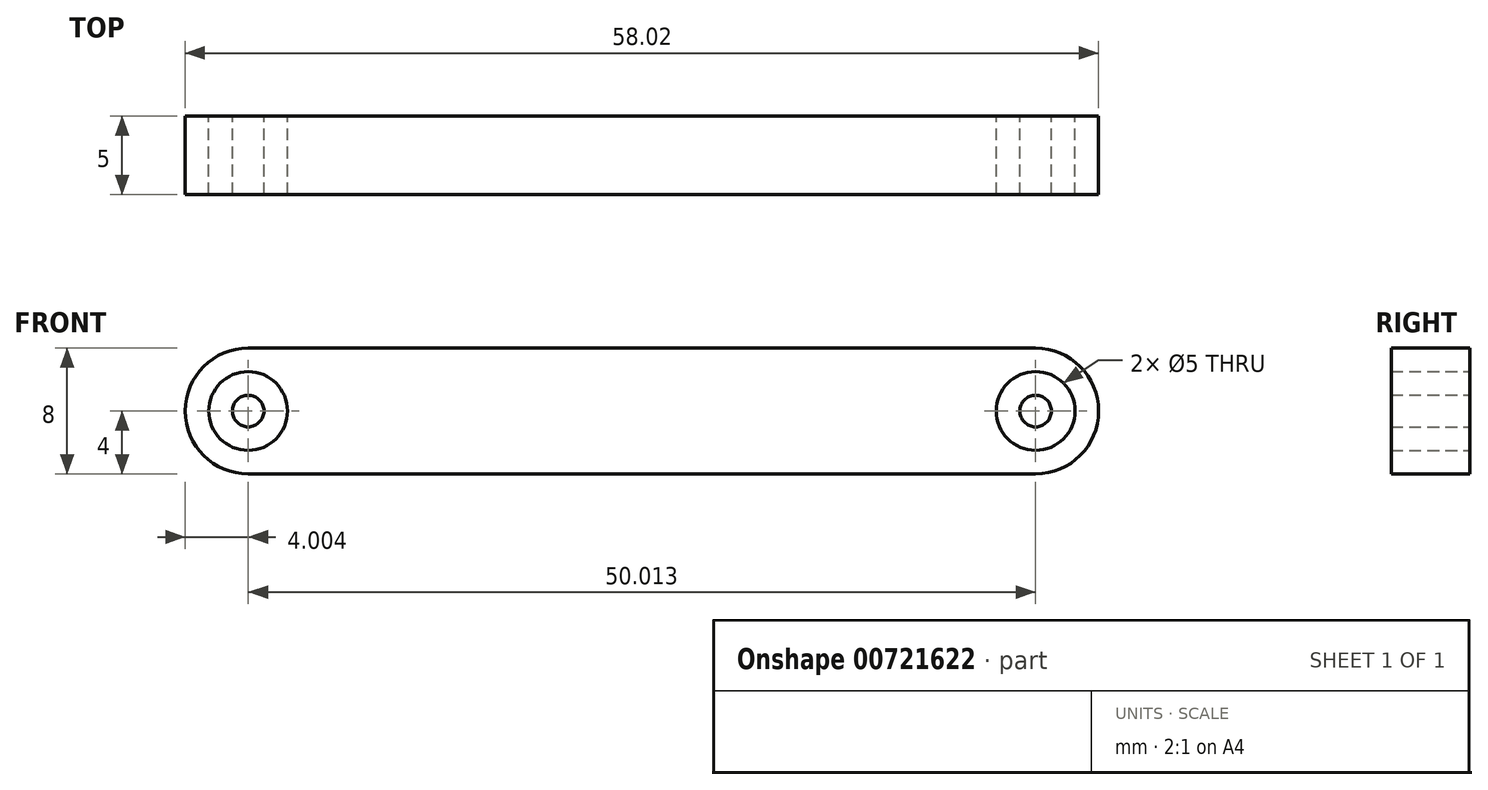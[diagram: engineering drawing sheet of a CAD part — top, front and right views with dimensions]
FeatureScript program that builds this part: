
annotation { "Feature Type Name" : "Feature", "Feature Type Description" : "" }
export const myFeature = defineFeature(function(context is Context, id is Id, definition is map)
    precondition{}
    {
        {
            var Q0;
            Q0=qCreatedBy(makeId("Front.planeOp"),FACE);
            var sketch = newSketch(context, id + "F0", { "sketchPlane" : qUnion([Q0])});
            skLineSegment(sketch, "E0.bottom", {"start": v(25, 4) * mm, "end": v(-25, 4) * mm});
            skLineSegment(sketch, "E0.top", {"start": v(25, -4) * mm, "end": v(-25, -4) * mm});
            skPoint(sketch, "E0.middle", {"position": v(0, 0) * mm});
            skArc(sketch, "E1", {"start": v(-25, 4) * mm, "mid": v(-29, 0) * mm, "end": v(-25, -4) * mm});
            skArc(sketch, "E2", {"start": v(25, -4) * mm, "mid": v(29, 0) * mm, "end": v(25, 4) * mm});
            skCircle(sketch, "E3", {"center": v(25, 0) * mm, "radius": 2.5 * mm});
            skCircle(sketch, "E4", {"center": v(25, 0) * mm, "radius": 1 * mm});
            skCircle(sketch, "E5", {"center": v(-25, 0) * mm, "radius": 2.5 * mm});
            skCircle(sketch, "E6", {"center": v(-25, 0) * mm, "radius": 1 * mm});
            skSolve(sketch);
        }
        {
            var Q0;
            Q0 = qSketchRegion(id + "F0", true);
            var Q1;
            Q1=makeQuery(id+"F0.imprint","IMPRINT",FACE,{"disambiguationData":[TD([[makeQuery(id+"F0.imprint","IMPRINT",EDGE,{"derivedFrom":sQuery(id+"F0.wireOp",EDGE,"E6")}),1.0]])]});
            var Q2;
            Q2=makeQuery(id+"F0.imprint","IMPRINT",FACE,{"disambiguationData":[TD([[makeQuery(id+"F0.imprint","IMPRINT",EDGE,{"derivedFrom":sQuery(id+"F0.wireOp",EDGE,"E4")}),1.0]])]});
            extrude(context, id + "F1", {"entities" : qUnion([Q0, Q1, Q2]), "endBound" : BoundingType.SYMMETRIC, "depth" : 5 * mm, "offsetDistance" : 25.4 * mm});
        }
    });
